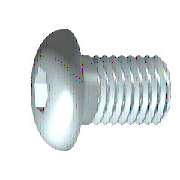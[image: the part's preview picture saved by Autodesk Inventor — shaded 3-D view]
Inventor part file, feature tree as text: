
AUTODESK INVENTOR PART (.ipt)
format: ipt  version: 2023.5 (Build 275446000, 446)  size: 193,536 bytes
history: native  units: mm (DEFAULTED — no unit token found)
features: extrude x1, plane x1, fillet x1
ambient origin geometry x7: Origin, YZ Plane, XY Plane, X Axis, Y Axis, Z Axis, Center Point
bodies: Solid1 (feature_tree), Body (feature_tree)
feature tree (3):
  extrude  "Slot"  Depth=11.112246mm
  plane  "Work Plane1"
  fillet  "Fillet2"  Radius=1.5876mm
